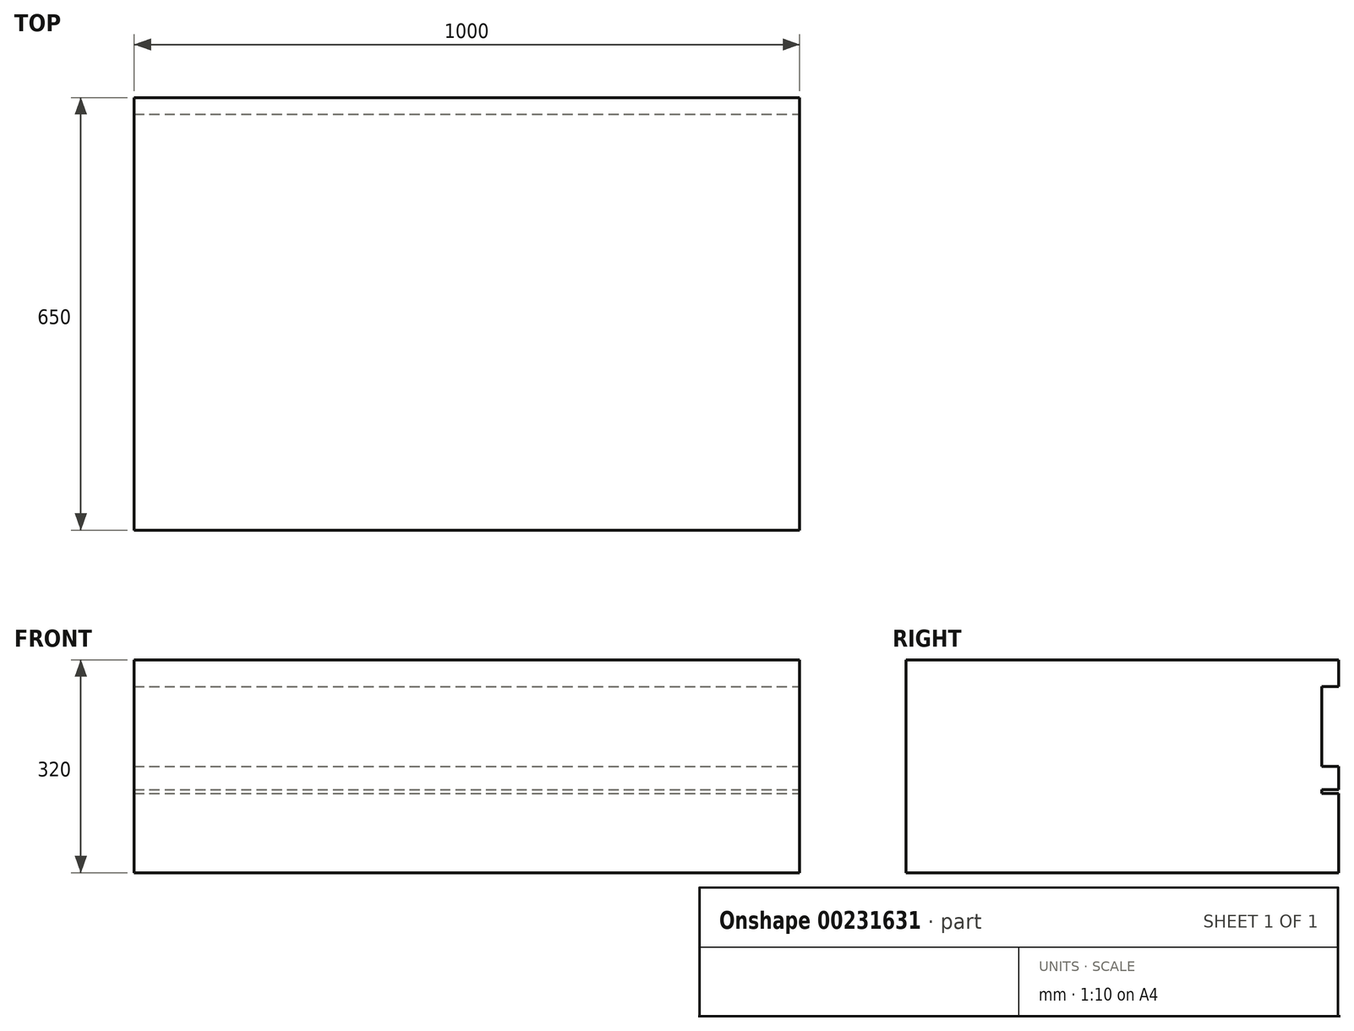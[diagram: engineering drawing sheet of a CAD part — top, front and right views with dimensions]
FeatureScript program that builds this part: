
annotation { "Feature Type Name" : "Feature", "Feature Type Description" : "" }
export const myFeature = defineFeature(function(context is Context, id is Id, definition is map)
    precondition{}
    {
        {
            var Q0;
            Q0=qCreatedBy(makeId("Front.planeOp"),FACE);
            var sketch = newSketch(context, id + "F0", { "sketchPlane" : qUnion([Q0])});
            skLineSegment(sketch, "E0.bottom", {"start": v(0, 0) * mm, "end": v(1000, 0) * mm});
            skLineSegment(sketch, "E0.top", {"start": v(0, 320) * mm, "end": v(1000, 320) * mm});
            skLineSegment(sketch, "E0.left", {"start": v(0, 0) * mm, "end": v(0, 320) * mm});
            skLineSegment(sketch, "E0.right", {"start": v(1000, 0) * mm, "end": v(1000, 320) * mm});
            skSolve(sketch);
        }
        {
            var Q0;
            Q0=qSketchRegion(id+"F0",true);
            extrude(context, id + "F1", {"entities" : qUnion([Q0]), "depth" : 650 * mm});
        }
        {
            var Q0;
            Q0=makeQuery(id+"F1.opExtrude","CAP_FACE",FACE,{"disambiguationData":[OSD([sQuery(id+"F0.wireOp",EDGE,"E0.bottom"),sQuery(id+"F0.wireOp",EDGE,"E0.top"),sQuery(id+"F0.wireOp",EDGE,"E0.left"),sQuery(id+"F0.wireOp",EDGE,"E0.right")])],"isStart":true});
            var sketch = newSketch(context, id + "F2", { "sketchPlane" : qUnion([Q0])});
            skLineSegment(sketch, "E1", {"start": v(0, 280) * mm, "end": v(-1000, 280) * mm});
            skLineSegment(sketch, "E2", {"start": v(0, 160) * mm, "end": v(-1000, 160) * mm});
            skLineSegment(sketch, "E3", {"start": v(0, 125) * mm, "end": v(-1000, 125) * mm});
            skPoint(sketch, "E3.endSnap0", {"position": v(-1000, 160) * mm});
            skSolve(sketch);
        }
        {
            var Q0;
            {var subQ0=sQuery(id+"F2.wireOp",EDGE,"E1");Q0=makeQuery(id+"F2.imprint","IMPRINT",FACE,{"disambiguationData":[TD([[makeQuery(id+"F2.imprint","IMPRINT",EDGE,{"derivedFrom":subQ0}),1.0]])]});}
            var Q1;
            {var subQ0=sQuery(id+"F2.wireOp",EDGE,"E3");Q1=makeQuery(id+"F2.imprint","IMPRINT",FACE,{"disambiguationData":[TD([[makeQuery(id+"F2.imprint","IMPRINT",EDGE,{"derivedFrom":subQ0}),1.0]])]});}
            extrude(context, id + "F3", {"entities" : qUnion([Q0, Q1]), "operationType" : NewBodyOperationType.ADD, "oppositeDirection" : true, "depth" : 28 * mm});
        }
        {
            var Q0;
            {var subQ0=sQuery(id+"F2.wireOp",EDGE,"E1");Q0=makeQuery(id+"F2.imprint","IMPRINT",FACE,{"disambiguationData":[TD([[makeQuery(id+"F2.imprint","IMPRINT",EDGE,{"derivedFrom":subQ0}),1.0]])]});}
            extrude(context, id + "F4", {"entities" : qUnion([Q0]), "operationType" : NewBodyOperationType.REMOVE, "oppositeDirection" : true, "depth" : 25 * mm});
        }
        {
            var Q0;
            {var subQ0=sQuery(id+"F0.wireOp",EDGE,"E0.bottom");var subQ1=sQuery(id+"F0.wireOp",EDGE,"E0.left");var subQ2=sQuery(id+"F0.wireOp",EDGE,"E0.right");Q0=makeQuery(id+"F4.boolean.opBoolean","SPLIT",FACE,{"disambiguationData":[TD([makeQuery(id+"F1.opExtrude","SWEPT_FACE",FACE,{"disambiguationData":[OSD([subQ0])]})])],"derivedFrom":makeQuery(id+"F1.opExtrude","CAP_FACE",FACE,{"disambiguationData":[OSD([subQ0,sQuery(id+"F0.wireOp",EDGE,"E0.top"),subQ1,subQ2])],"isStart":true})});}
            var sketch = newSketch(context, id + "F5", { "sketchPlane" : qUnion([Q0])});
            skLineSegment(sketch, "E4", {"start": v(0, 125) * mm, "end": v(-1000, 125) * mm});
            skLineSegment(sketch, "E5", {"start": v(0, 118.86) * mm, "end": v(-1000, 118.86) * mm});
            skSolve(sketch);
        }
        {
            var Q0;
            {var subQ0=sQuery(id+"F5.wireOp",EDGE,"E4");Q0=makeQuery(id+"F5.imprint","IMPRINT",FACE,{"disambiguationData":[TD([[makeQuery(id+"F5.imprint","IMPRINT",EDGE,{"derivedFrom":subQ0}),1.0]])]});}
            extrude(context, id + "F6", {"entities" : qUnion([Q0]), "operationType" : NewBodyOperationType.REMOVE, "oppositeDirection" : true, "depth" : 25 * mm});
        }
    });
